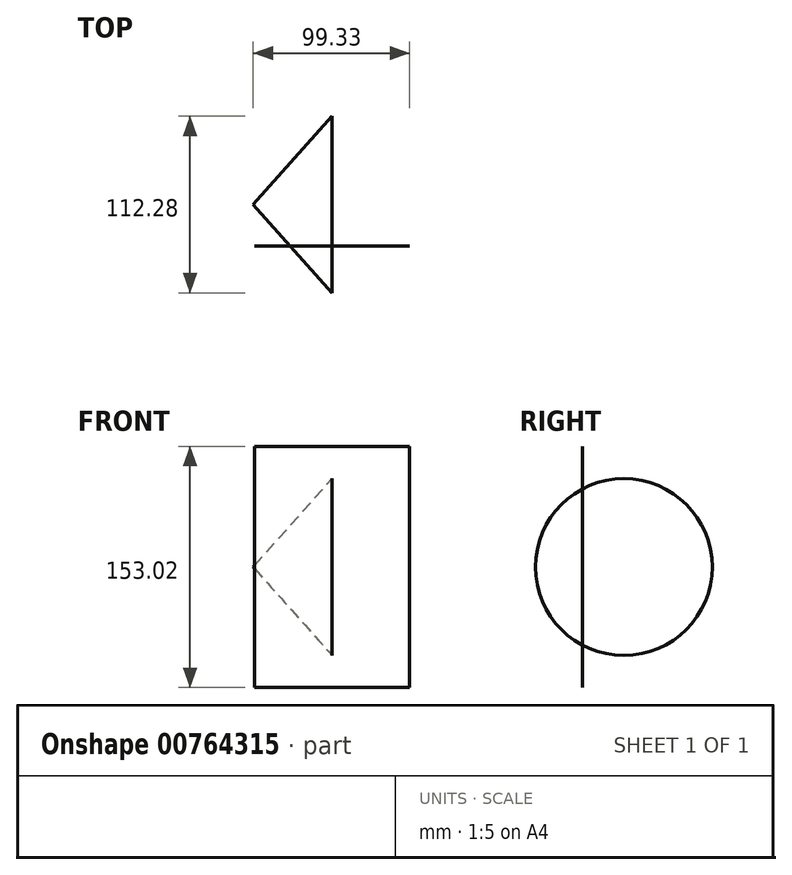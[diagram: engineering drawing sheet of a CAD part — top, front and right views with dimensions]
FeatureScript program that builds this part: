
annotation { "Feature Type Name" : "Feature", "Feature Type Description" : "" }
export const myFeature = defineFeature(function(context is Context, id is Id, definition is map)
    precondition{}
    {
        {
            var Q0;
            Q0=qCreatedBy(makeId("Front.planeOp"),FACE);
            var sketch = newSketch(context, id + "F0", { "sketchPlane" : qUnion([Q0])});
            skLineSegment(sketch, "E0", {"start": v(0, 56.14) * mm, "end": v(-50.05, 0) * mm});
            skLineSegment(sketch, "E1", {"start": v(-50.05, 0) * mm, "end": v(0, 0) * mm});
            skLineSegment(sketch, "E2", {"start": v(0, 0) * mm, "end": v(0, 56.14) * mm});
            skSolve(sketch);
        }
        {
            var Q0;
            Q0=sQuery(id+"F0.wireOp",EDGE,"E0");
            var Q1;
            Q1=sQuery(id+"F0.wireOp",EDGE,"E1");
            revolve(context, id + "F1", {"bodyType" : ToolBodyType.SURFACE, "surfaceOperationType" : NewSurfaceOperationType.NEW, "surfaceEntities" : qUnion([Q0]), "axis" : qUnion([Q1]), "revolveType" : RevolveType.FULL});
        }
        {
            var Q0;
            Q0=qCreatedBy(makeId("Right.planeOp"),FACE);
            var sketch = newSketch(context, id + "F2", { "sketchPlane" : qUnion([Q0])});
            skLineSegment(sketch, "E3", {"start": v(-26.45, 76.6) * mm, "end": v(-26.45, -76.42) * mm});
            skSolve(sketch);
        }
        {
            var Q0;
            Q0=sQuery(id+"F2.wireOp",EDGE,"E3");
            extrude(context, id + "F3", {"bodyType" : ToolBodyType.SURFACE, "surfaceOperationType" : NewSurfaceOperationType.ADD, "surfaceEntities" : qUnion([Q0]), "endBound" : BoundingType.SYMMETRIC, "depth" : 98.55 * mm, "offsetDistance" : 25.4 * mm});
        }
    });
